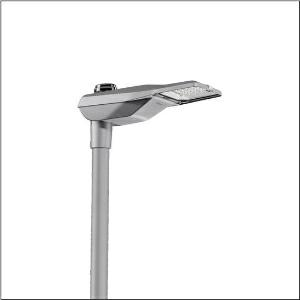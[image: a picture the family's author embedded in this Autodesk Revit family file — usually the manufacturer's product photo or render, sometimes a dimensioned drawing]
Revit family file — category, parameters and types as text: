
# Revit family: streetlight_sl_21_micro___st0_8a_5xe5c37n08db_0c9a
name_source: partatom
category: Lighting Fixtures
units: mm (PartAtom-declared; Revit-internal decimal feet)

## family parameters
Cut with Voids When Loaded = No
Host = Face
Light Source = No
Part Type = Normal
Room Calculation Point = No
Round Connector Dimension = Use Diameter
Shared = No

## types (1)
- --- (1 x LED, 5110 lm, 39.1 W, 3000K)
    Apparent Load = 39 VA
    CIE Flux Codes = 38 75 97 100 100
    Color Rendering = 70
    Color Temperature = 3000K
    Default Elevation = 1800 mm
    Description = Streetlight SL 21 micro, mast luminaire, primary light control with lens, of PMMA, primary optical cover: cover, of toughened safety glass, transparent, light distribution: ST0.8a, light emission: direct distribution, primary light characteristic: asymmetric, installation type: post-top, LED, 3G 1.5mm², High Power LED, rated luminous flux: 5.110lm, luminous efficacy: 131lm/W, light colour: 730, colour temperature: 3000K, control: overheat protection, presetting dimming linear, constant luminous flux control, time-dependent luminous flux control, flexible luminous flux parameterisation, mains connection: 230..240V, AC, 50/60Hz, connection cable pre-assembled, cable length: 6,5m, wiring characteristics: H07RN-F, start of lifetime: 39W, end of service life: 41W, reduction: 18W, luminaire housing, of diecast aluminium (EN AC-44300), powder-coated, Siteco® metallic grey (DB 702S), corrosivity category C5 mid according to DIN EN ISO 12944, multi-level sealing system, sealing non-destructively replaceable, inclination adjustable: 0°, 5°, 10°, 15°, length: 528mm, width: 235mm, height: 110mm, spigot size: 76/60mm (post-top), protection rating (complete): IP66, insulation class (complete): insulation class I (protective earthing), certification: CE, ENEC, ENEC+, VDE, impact resistance: IK09, permissible operating ambient temperature for outdoor applications: -40..+50°C, standard-compliant lighting for roads and squares, packaging unit: 1 piece

Light Distribution: ST0.8a
    Height = 110 mm
    Lamp = 1 x LED
    Lamp Light Flux = 5110 lm
    Lamp Power = 39.1 W
    Lamp count = 1
    Length = 528 mm
    Luminous efficacy = 131 lm/W
    Manufacturer = Siteco
    ModVariant = No
    Model = 5XE5C37N08DB
    Number of Poles = 1
    OnlyDefault = Yes
    Power Factor = 1
    Product Name = Streetlight SL 21 micro | ST0.8a
    Product group = mast luminaire | pylon top
    ProductGroupID = 6100
    Protection Class = Protection class I
    Protection Degree = IP 66
    RLX_Detail_Level = 1
    RLX_Emergency_Light_Flux = 0 lm
    RLX_Emergency_Type = 0
    RLX_Emergency_Type_DB = No
    RlxData = <blob elided: 99025 chars, md5=00db79cc>
    Socket = socket
    Standby Power = 0 W
    System Light Flux = 5110 lm
    System Power = 39 W
    Type Comments = factory setting: luminous flux: 100 % | dim-lin: 254 | 765 mA
    Type Image = l_1294375.jpg
    URL = http://relux.com
    VarID = @adj_083751
    Voltage = 0 V
    Weight = 0.00 kg
    Width = 235 mm

## geometry (parser evidence)
native form markers: Blend x4, Sweep x11
no freeform markers — native parametric forms only
